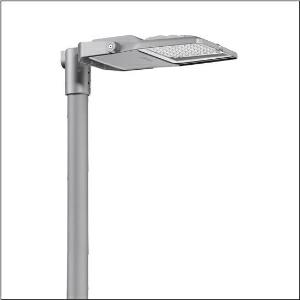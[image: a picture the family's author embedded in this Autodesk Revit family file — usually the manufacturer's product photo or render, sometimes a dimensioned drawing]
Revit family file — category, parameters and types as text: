
# Revit family: floodlight_fl_21_iq_mini___pl52_5xa7772c4d3a_40ba
name_source: partatom
category: Lighting Fixtures
units: mm (PartAtom-declared; Revit-internal decimal feet)

## family parameters
Cut with Voids When Loaded = No
Host = Face
Light Source = No
Part Type = Normal
Room Calculation Point = No
Round Connector Dimension = Use Diameter
Shared = No

## types (1)
- --- (1 x LED, 12720 lm, 87.2 W, 4000K)
    Apparent Load = 87 VA
    CIE Flux Codes = 26 60 98 100 100
    Color Rendering = 70
    Color Temperature = 4000K
    Default Elevation = 1800 mm
    Description = Floodlight FL 21 iQ mini, floodlight, primary light control with lens, of PMMA, primary optical cover: protective disc, of toughened safety glass, transparent, light distribution: PL52, light emission: direct distribution, installation type: surface-mounted, LED, High Power LED, rated luminous flux: 12.720lm, luminous efficacy: 146lm/W, light colour: 740, colour temperature: 4000K, control: Auto-Match, Temp-Guard, Night-Set, Smart-Wire, Desk-Remote (wireless, voltage-free reading and setting of iQ features in the workshop via application-optimized NFC function/RFID function), optimised constant luminous flux control (CLO 2.0), Light-Fading, Lumen-Switch, with terminal, 6-pole, mains connection: 220..240V, AC, 50/60Hz, start of lifetime: 87W, end of service life: 92W, reduction: 40W, luminaire housing, of diecast aluminium, powder-coated, Siteco® metallic grey (DB 702S), corrosivity category C5 mid according to DIN EN ISO 12944, sealing non-destructively replaceable, please order mast flange separately, mast bracket, of steel, galvanised, powder-coated, protection rating (complete): IP66, insulation class (complete): insulation class II (safety insulation), certification: CE, ENEC, VDE, protection symbol: D, impact resistance: IK08, permissible operating ambient temperature: -40..+40°C, permissible operating ambient temperature for outdoor applications: -40..+50°C, standard: DIN EN 12944, LABS conformity tested according to VDMA 24364:2018-05, packaging unit: 1 piece

Light Distribution: PL52
    Height = 70 mm
    Lamp = 1 x LED
    Lamp Light Flux = 12720 lm
    Lamp Power = 87.2 W
    Lamp count = 1
    Length = 485 mm
    Luminous efficacy = 146 lm/W
    Manufacturer = Siteco
    ModVariant = No
    Model = 5XA7772C4D3A
    Number of Poles = 1
    OnlyDefault = Yes
    Power Factor = 1
    Product Name = Floodlight FL 21 iQ mini | PL52
    Product group = floodlight | pylon annexe
    ProductGroupID = 6200
    Protection Class = Protection class II
    Protection Degree = IP 66
    RLX_Detail_Level = 1
    RLX_Emergency_Light_Flux = 0 lm
    RLX_Emergency_Type = 0
    RLX_Emergency_Type_DB = No
    RlxData = <blob elided: 101561 chars, md5=3a2d795e>
    Socket = socket
    Standby Power = 0 W
    System Light Flux = 12720 lm
    System Power = 87 W
    Type Comments = factory setting: luminous flux: 100 % | dim-lin: 254 | 456 mA
    Type Image = l_1007125.jpg
    URL = http://relux.com
    VarID = @adj_114311
    Voltage = 0 V
    Weight = 0.00 kg
    Width = 337 mm

## geometry (parser evidence)
native form markers: Blend x4, Sweep x14
no freeform markers — native parametric forms only
